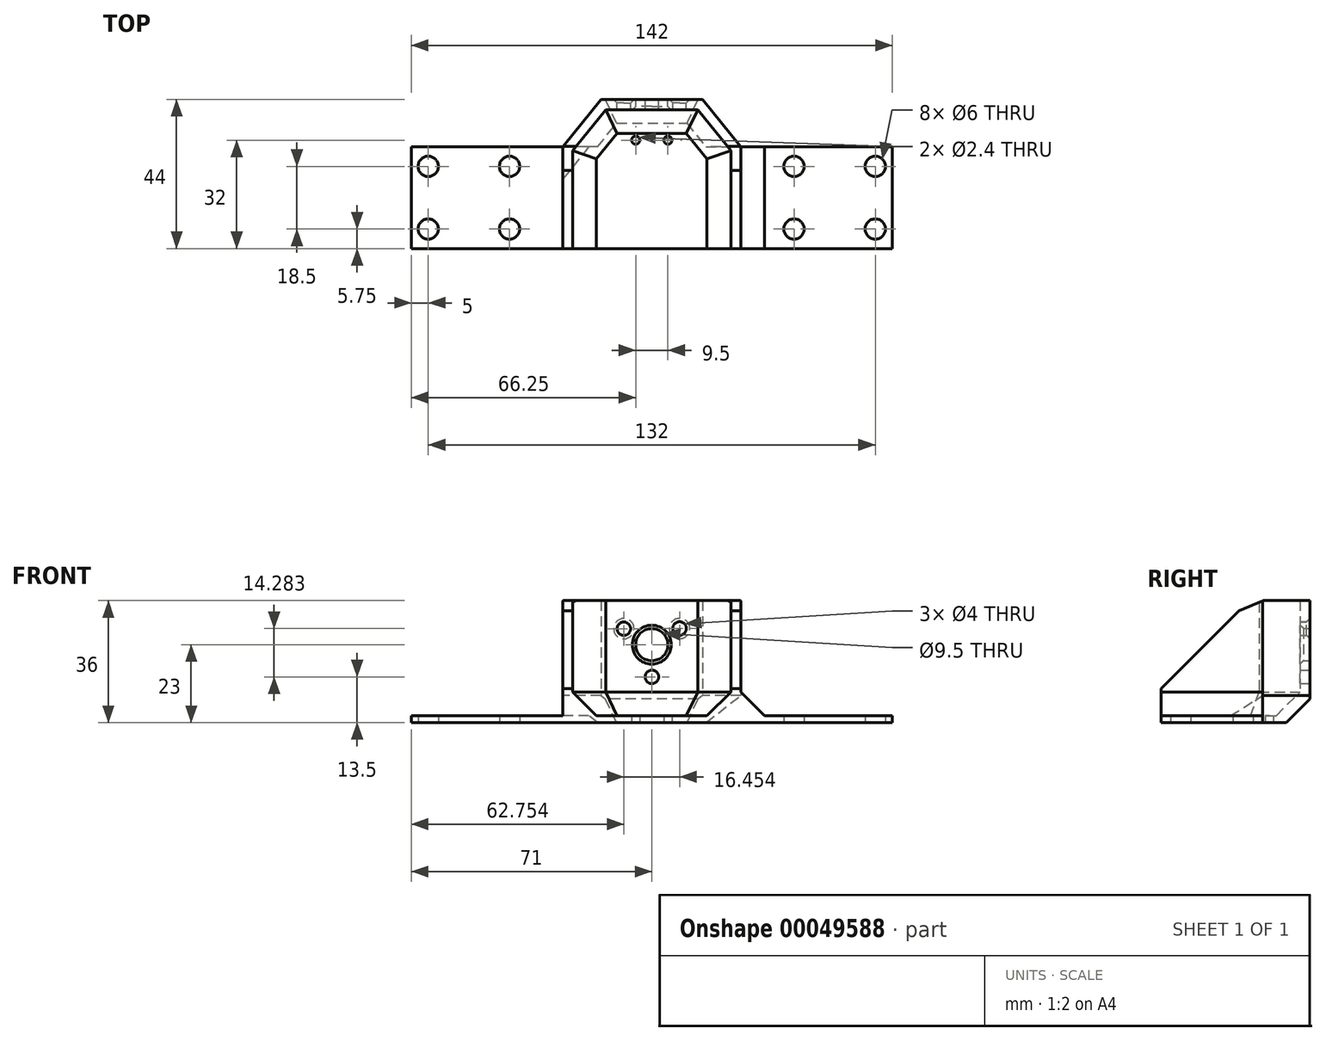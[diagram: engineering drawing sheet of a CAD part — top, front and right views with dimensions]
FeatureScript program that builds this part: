
annotation { "Feature Type Name" : "Feature", "Feature Type Description" : "" }
export const myFeature = defineFeature(function(context is Context, id is Id, definition is map)
    precondition{}
    {
        {
            var Q0;
            Q0=qCreatedBy(makeId("Top.planeOp"),FACE);
            var sketch = newSketch(context, id + "F0", { "sketchPlane" : qUnion([Q0])});
            skPoint(sketch, "E0.rect.middle", {"position": v(0, 0) * mm});
            skCircle(sketch, "E1", {"center": v(-42, 9.25) * mm, "radius": 3 * mm});
            skCircle(sketch, "E2", {"center": v(-66, 9.25) * mm, "radius": 3 * mm});
            skCircle(sketch, "E3", {"center": v(-66, -9.25) * mm, "radius": 3 * mm});
            skCircle(sketch, "E4", {"center": v(-42, -9.25) * mm, "radius": 3 * mm});
            skCircle(sketch, "E5", {"center": v(42, -9.25) * mm, "radius": 3 * mm});
            skCircle(sketch, "E6", {"center": v(66, -9.25) * mm, "radius": 3 * mm});
            skCircle(sketch, "E7", {"center": v(66, 9.25) * mm, "radius": 3 * mm});
            skCircle(sketch, "E8", {"center": v(42, 9.25) * mm, "radius": 3 * mm});
            skLineSegment(sketch, "E9.rect.bottom", {"start": v(71, -15) * mm, "end": v(-71, -15) * mm});
            skLineSegment(sketch, "E9.rect.top", {"start": v(71, 15) * mm, "end": v(26.31, 15) * mm});
            skLineSegment(sketch, "E9.rect.left", {"start": v(71, -15) * mm, "end": v(71, 15) * mm});
            skLineSegment(sketch, "E9.rect.right", {"start": v(-71, -15) * mm, "end": v(-71, 15) * mm});
            skLineSegment(sketch, "E10.rect.bottom", {"start": v(15, 29) * mm, "end": v(-15, 29) * mm});
            skPoint(sketch, "E10.rect.middle", {"position": v(0, 15) * mm});
            skPoint(sketch, "E10.rect.top.start.orphan", {"position": v(15, 1) * mm});
            skPoint(sketch, "E11.orphan", {"position": v(-15, 1) * mm});
            skLineSegment(sketch, "E12.trimOffspring", {"start": v(-26.31, 15) * mm, "end": v(-71, 15) * mm});
            skLineSegment(sketch, "E13", {"start": v(-15, 29) * mm, "end": v(-26.31, 15) * mm});
            skLineSegment(sketch, "E14", {"start": v(15, 29) * mm, "end": v(26.31, 15) * mm});
            skSolve(sketch);
        }
        {
            var Q0;
            Q0=makeQuery(id+"F0.imprint","IMPRINT",FACE,{"disambiguationData":[TD([[makeQuery(id+"F0.imprint","IMPRINT",EDGE,{"derivedFrom":sQuery(id+"F0.wireOp",EDGE,"E1")}),-1.0]])]});
            extrude(context, id + "F1", {"entities" : qUnion([Q0]), "depth" : 2 * mm});
        }
        {
            var Q0;
            Q0=makeQuery(id+"F1.opExtrude","CAP_FACE",FACE,{"disambiguationData":[OSD([sQuery(id+"F0.wireOp",EDGE,"E1"),sQuery(id+"F0.wireOp",EDGE,"E2"),sQuery(id+"F0.wireOp",EDGE,"E3"),sQuery(id+"F0.wireOp",EDGE,"E4"),sQuery(id+"F0.wireOp",EDGE,"E5"),sQuery(id+"F0.wireOp",EDGE,"E6"),sQuery(id+"F0.wireOp",EDGE,"E7"),sQuery(id+"F0.wireOp",EDGE,"E8"),sQuery(id+"F0.wireOp",EDGE,"E9.rect.bottom"),sQuery(id+"F0.wireOp",EDGE,"E9.rect.top"),sQuery(id+"F0.wireOp",EDGE,"E9.rect.left"),sQuery(id+"F0.wireOp",EDGE,"E9.rect.right"),sQuery(id+"F0.wireOp",EDGE,"E10.rect.bottom"),sQuery(id+"F0.wireOp",EDGE,"E12.trimOffspring"),sQuery(id+"F0.wireOp",EDGE,"E13"),sQuery(id+"F0.wireOp",EDGE,"E14")])],"isStart":false});
            var sketch = newSketch(context, id + "F2", { "sketchPlane" : qUnion([Q0])});
            skLineSegment(sketch, "E15", {"start": v(-26.31, 15) * mm, "end": v(-26.31, -15) * mm});
            skLineSegment(sketch, "E16", {"start": v(26.31, 15) * mm, "end": v(26.31, -15) * mm});
            skLineSegment(sketch, "E17.0", {"start": v(-23.31, 13.94) * mm, "end": v(-23.31, -15) * mm});
            skLineSegment(sketch, "E17.1", {"start": v(23.31, 13.94) * mm, "end": v(23.31, -15) * mm});
            skLineSegment(sketch, "E17.2", {"start": v(13.57, 26) * mm, "end": v(23.31, 13.94) * mm});
            skLineSegment(sketch, "E17.3", {"start": v(13.57, 26) * mm, "end": v(-13.57, 26) * mm});
            skLineSegment(sketch, "E17.4", {"start": v(-13.57, 26) * mm, "end": v(-23.31, 13.94) * mm});
            skSolve(sketch);
        }
        {
            var Q0;
            {var subQ2=sQuery(id+"F2.wireOp",EDGE,"E15");Q0=makeQuery(id+"F2.imprint","IMPRINT",FACE,{"disambiguationData":[TD([[makeQuery(id+"F2.imprint","IMPRINT",EDGE,{"derivedFrom":subQ2}),1.0]])]});}
            extrude(context, id + "F3", {"entities" : qUnion([Q0]), "operationType" : NewBodyOperationType.ADD, "depth" : 21 * mm});
        }
        {
            var Q0;
            {var subQ0=sQuery(id+"F0.wireOp",EDGE,"E10.rect.bottom");Q0=makeQuery(id+"F3.boolean.opBoolean","MERGE",FACE,{"derivedFrom":[makeQuery(id+"F1.opExtrude","SWEPT_FACE",FACE,{"disambiguationData":[OSD([subQ0])]}),makeQuery(id+"F3.opExtrude","SWEPT_FACE",FACE,{"disambiguationData":[OSD([subQ0])]})]});}
            var sketch = newSketch(context, id + "F4", { "sketchPlane" : qUnion([Q0])});
            skCircle(sketch, "E18", {"center": v(0, 23) * mm, "radius": 4.75 * mm});
            skLineSegment(sketch, "E19", {"start": v(0, 36) * mm, "end": v(-15, 36) * mm});
            skLineSegment(sketch, "E20", {"start": v(-15, 36) * mm, "end": v(-15, 23) * mm});
            skLineSegment(sketch, "E21", {"start": v(0, 36) * mm, "end": v(15, 36) * mm});
            skLineSegment(sketch, "E22", {"start": v(15, 36) * mm, "end": v(15, 23) * mm});
            skLineSegment(sketch, "E23", {"start": v(-15, 23) * mm, "end": v(-4.75, 23) * mm});
            skLineSegment(sketch, "E24.trimOffspring", {"start": v(4.75, 23) * mm, "end": v(15, 23) * mm});
            skCircle(sketch, "E25.cCircle", {"center": v(0, 23) * mm, "radius": 4.84 * mm, "construction": true});
            skPoint(sketch, "E25.0.midPoint", {"position": v(0, 18.16) * mm});
            skCircle(sketch, "E26", {"center": v(8.25, 27.72) * mm, "radius": 2 * mm});
            skCircle(sketch, "E27.1.0", {"center": v(-8.2, 27.78) * mm, "radius": 2 * mm});
            skCircle(sketch, "E27.2.0", {"center": v(-0.04, 13.5) * mm, "radius": 2 * mm});
            skPoint(sketch, "E25.0.start.orphan", {"position": v(8.38, 18.16) * mm});
            skPoint(sketch, "E25.1.start.orphan", {"position": v(-8.37, 18.16) * mm});
            skSolve(sketch);
        }
        {
            var Q0;
            Q0=makeQuery(id+"F4.imprint","IMPRINT",FACE,{"disambiguationData":[TD([[makeQuery(id+"F4.imprint","IMPRINT",EDGE,{"derivedFrom":sQuery(id+"F4.wireOp",EDGE,"E19")}),1.0]])]});
            extrude(context, id + "F5", {"entities" : qUnion([Q0]), "operationType" : NewBodyOperationType.ADD, "oppositeDirection" : true, "depth" : 3 * mm});
        }
        {
            var Q0;
            Q0=makeQuery(id+"F4.imprint","IMPRINT",FACE,{"disambiguationData":[TD([[makeQuery(id+"F4.imprint","IMPRINT",EDGE,{"derivedFrom":sQuery(id+"F4.wireOp",EDGE,"E27.1.0")}),1.0]])]});
            var Q1;
            {var subQ0=makeQuery(id+"F3.opExtrude","CAP_EDGE",EDGE,{"disambiguationData":[OSD([sQuery(id+"F0.wireOp",EDGE,"E10.rect.bottom")])],"isStart":false});var subQ1=sQuery(id+"F4.wireOp",EDGE,"E18");var subQ3=makeQuery(id+"F4.imprint","INTERSECT",VERTEX,{"derivedFrom":[subQ0,subQ1,sQuery(id+"F4.wireOp",EDGE,"E23")]});Q1=makeQuery(id+"F4.imprint","IMPRINT",FACE,{"disambiguationData":[TD([[makeQuery(id+"F4.imprint","IMPRINT",EDGE,{"disambiguationData":[TD([[subQ3,-1.0]])],"derivedFrom":subQ1}),1.0]])]});}
            var Q2;
            Q2=makeQuery(id+"F4.imprint","IMPRINT",FACE,{"disambiguationData":[TD([[makeQuery(id+"F4.imprint","IMPRINT",EDGE,{"derivedFrom":sQuery(id+"F4.wireOp",EDGE,"E27.2.0")}),1.0]])]});
            extrude(context, id + "F6", {"entities" : qUnion([Q0, Q1, Q2]), "operationType" : NewBodyOperationType.REMOVE, "endBound" : BoundingType.THROUGH_ALL, "oppositeDirection" : true, "depth" : 25 * mm});
        }
        {
            var Q0;
            Q0=makeQuery(id+"F3.opExtrude","CAP_EDGE",EDGE,{"disambiguationData":[OSD([sQuery(id+"F2.wireOp",EDGE,"E15")])],"isStart":true});
            var Q1;
            Q1=makeQuery(id+"F3.opExtrude","CAP_EDGE",EDGE,{"disambiguationData":[OSD([sQuery(id+"F2.wireOp",EDGE,"E17.1")])],"isStart":true});
            var Q2;
            Q2=makeQuery(id+"F3.opExtrude","CAP_EDGE",EDGE,{"disambiguationData":[OSD([sQuery(id+"F2.wireOp",EDGE,"E17.2")])],"isStart":true});
            var Q3;
            Q3=makeQuery(id+"F3.opExtrude","CAP_EDGE",EDGE,{"disambiguationData":[OSD([sQuery(id+"F2.wireOp",EDGE,"E17.4")])],"isStart":true});
            var Q4;
            Q4=makeQuery(id+"F3.opExtrude","CAP_EDGE",EDGE,{"disambiguationData":[OSD([sQuery(id+"F2.wireOp",EDGE,"E17.0")])],"isStart":true});
            var Q5;
            Q5=makeQuery(id+"F3.opExtrude","CAP_EDGE",EDGE,{"disambiguationData":[OSD([sQuery(id+"F2.wireOp",EDGE,"E16")])],"isStart":true});
            var Q6;
            Q6=makeQuery(id+"F3.opExtrude","CAP_EDGE",EDGE,{"disambiguationData":[OSD([sQuery(id+"F2.wireOp",EDGE,"E17.3")])],"isStart":true});
            var Q7;
            Q7=makeQuery(id+"F1.opExtrude","CAP_EDGE",EDGE,{"disambiguationData":[OSD([sQuery(id+"F0.wireOp",EDGE,"E10.rect.bottom")])],"isStart":true});
            chamfer(context, id + "F7", {"entities" : qUnion([Q0, Q1, Q2, Q3, Q4, Q5, Q6, Q7]), "width" : 7 * mm, "tangentPropagation" : true});
        }
        {
            var Q0;
            {var subQ0=sQuery(id+"F0.wireOp",EDGE,"E9.rect.bottom");var subQ1=sQuery(id+"F0.wireOp",EDGE,"E10.rect.bottom");var subQ2=sQuery(id+"F0.wireOp",EDGE,"E13");var subQ3=sQuery(id+"F2.wireOp",EDGE,"E15");var subQ4=sQuery(id+"F2.wireOp",EDGE,"E16");var subQ5=sQuery(id+"F2.wireOp",EDGE,"E17.0");var subQ6=sQuery(id+"F2.wireOp",EDGE,"E17.1");var subQ7=sQuery(id+"F2.wireOp",EDGE,"E17.3");var subQ8=sQuery(id+"F2.wireOp",EDGE,"E17.4");Q0=makeQuery(id+"F5.boolean.opBoolean","SPLIT",FACE,{"disambiguationData":[TD([makeQuery(id+"F1.opExtrude","SWEPT_FACE",FACE,{"disambiguationData":[OSD([subQ2])]})])],"derivedFrom":makeQuery(id+"F3.opExtrude","CAP_FACE",FACE,{"disambiguationData":[OSD([subQ0,subQ1,subQ2,sQuery(id+"F0.wireOp",EDGE,"E14"),subQ3,subQ4,subQ5,subQ6,sQuery(id+"F2.wireOp",EDGE,"E17.2"),subQ7,subQ8])],"isStart":false})});}
            var Q1;
            {var subQ0=sQuery(id+"F0.wireOp",EDGE,"E9.rect.bottom");var subQ1=sQuery(id+"F0.wireOp",EDGE,"E10.rect.bottom");var subQ2=sQuery(id+"F0.wireOp",EDGE,"E14");var subQ3=sQuery(id+"F2.wireOp",EDGE,"E15");var subQ4=sQuery(id+"F2.wireOp",EDGE,"E16");var subQ5=sQuery(id+"F2.wireOp",EDGE,"E17.0");var subQ6=sQuery(id+"F2.wireOp",EDGE,"E17.1");var subQ7=sQuery(id+"F2.wireOp",EDGE,"E17.2");var subQ8=sQuery(id+"F2.wireOp",EDGE,"E17.3");Q1=makeQuery(id+"F5.boolean.opBoolean","SPLIT",FACE,{"disambiguationData":[TD([makeQuery(id+"F1.opExtrude","SWEPT_FACE",FACE,{"disambiguationData":[OSD([subQ2])]})])],"derivedFrom":makeQuery(id+"F3.opExtrude","CAP_FACE",FACE,{"disambiguationData":[OSD([subQ0,subQ1,sQuery(id+"F0.wireOp",EDGE,"E13"),subQ2,subQ3,subQ4,subQ5,subQ6,subQ7,subQ8,sQuery(id+"F2.wireOp",EDGE,"E17.4")])],"isStart":false})});}
            extrude(context, id + "F8", {"entities" : qUnion([Q0, Q1]), "operationType" : NewBodyOperationType.ADD, "depth" : 13 * mm});
        }
        {
            var Q0;
            {var subQ0=sQuery(id+"F0.wireOp",EDGE,"E9.rect.bottom");var subQ1=makeQuery(id+"F1.opExtrude","CAP_EDGE",EDGE,{"disambiguationData":[OSD([subQ0])],"isStart":false});Q0=makeQuery(id+"F8.opExtrude","CAP_EDGE",EDGE,{"disambiguationData":[OSD([subQ0]),TDD([makeQuery(id+"F3.opExtrude","CAP_EDGE",EDGE,{"disambiguationData":[OSD([subQ0]),TDD([makeQuery(id+"F2.imprint","IMPRINT",EDGE,{"disambiguationData":[TD([[makeQuery(id+"F2.imprint","INTERSECT",VERTEX,{"derivedFrom":[subQ1,sQuery(id+"F2.wireOp",EDGE,"E15")]}),1.0]])],"derivedFrom":subQ1})])],"isStart":false})])],"isStart":false});}
            var Q1;
            {var subQ0=sQuery(id+"F0.wireOp",EDGE,"E9.rect.bottom");var subQ1=makeQuery(id+"F1.opExtrude","CAP_EDGE",EDGE,{"disambiguationData":[OSD([subQ0])],"isStart":false});Q1=makeQuery(id+"F8.opExtrude","CAP_EDGE",EDGE,{"disambiguationData":[OSD([subQ0]),TDD([makeQuery(id+"F3.opExtrude","CAP_EDGE",EDGE,{"disambiguationData":[OSD([subQ0]),TDD([makeQuery(id+"F2.imprint","IMPRINT",EDGE,{"disambiguationData":[TD([[makeQuery(id+"F2.imprint","INTERSECT",VERTEX,{"derivedFrom":[subQ1,sQuery(id+"F2.wireOp",EDGE,"E16")]}),-1.0]])],"derivedFrom":subQ1})])],"isStart":false})])],"isStart":false});}
            chamfer(context, id + "F9", {"entities" : qUnion([Q0, Q1]), "width" : 26 * mm, "tangentPropagation" : true});
        }
        {
            var Q0;
            {var subQ0=sQuery(id+"F0.wireOp",EDGE,"E9.rect.bottom");var subQ1=makeQuery(id+"F1.opExtrude","CAP_EDGE",EDGE,{"disambiguationData":[OSD([subQ0])],"isStart":false});var subQ2=sQuery(id+"F2.wireOp",EDGE,"E17.0");var subQ3=sQuery(id+"F2.wireOp",EDGE,"E15");var subQ4=makeQuery(id+"F2.imprint","IMPRINT",EDGE,{"disambiguationData":[TD([[makeQuery(id+"F2.imprint","INTERSECT",VERTEX,{"derivedFrom":[subQ1,subQ3]}),1.0]])],"derivedFrom":subQ1});var subQ5=sQuery(id+"F4.wireOp",EDGE,"E19");var subQ6=sQuery(id+"F4.wireOp",EDGE,"E21");var subQ7=sQuery(id+"F0.wireOp",EDGE,"E10.rect.bottom");var subQ8=sQuery(id+"F0.wireOp",EDGE,"E13");var subQ9=sQuery(id+"F0.wireOp",EDGE,"E14");var subQ10=sQuery(id+"F2.wireOp",EDGE,"E16");var subQ11=sQuery(id+"F2.wireOp",EDGE,"E17.1");var subQ12=sQuery(id+"F2.wireOp",EDGE,"E17.2");var subQ13=sQuery(id+"F2.wireOp",EDGE,"E17.3");var subQ14=sQuery(id+"F2.wireOp",EDGE,"E17.4");var subQ15=makeQuery(id+"F3.opExtrude","CAP_FACE",FACE,{"disambiguationData":[OSD([subQ0,subQ7,subQ8,subQ9,subQ3,subQ10,subQ2,subQ11,subQ12,subQ13,subQ14])],"isStart":false});Q0=makeQuery(id+"F9.opChamfer","BLEND_EDGE",EDGE,{"blendedFrom":[makeQuery(id+"F8.opExtrude","CAP_EDGE",EDGE,{"disambiguationData":[OSD([subQ0]),TDD([makeQuery(id+"F3.opExtrude","CAP_EDGE",EDGE,{"disambiguationData":[OSD([subQ0]),TDD([subQ4])],"isStart":false})])],"isStart":false}),makeQuery(id+"F8.boolean.opBoolean","MERGE",FACE,{"derivedFrom":[makeQuery(id+"F5.opExtrude","SWEPT_FACE",FACE,{"disambiguationData":[OSD([subQ5,subQ6])]}),makeQuery(id+"F8.opExtrude","CAP_FACE",FACE,{"disambiguationData":[OSD([subQ0,subQ7,subQ8,subQ9,subQ3,subQ10,subQ2,subQ11,subQ12,subQ13,subQ14]),TDD([makeQuery(id+"F5.boolean.opBoolean","SPLIT",FACE,{"disambiguationData":[TD([makeQuery(id+"F1.opExtrude","SWEPT_FACE",FACE,{"disambiguationData":[OSD([subQ8])]})])],"derivedFrom":subQ15})])],"isStart":false}),makeQuery(id+"F8.opExtrude","CAP_FACE",FACE,{"disambiguationData":[OSD([subQ0,subQ7,subQ8,subQ9,subQ3,subQ10,subQ2,subQ11,subQ12,subQ13,subQ14]),TDD([makeQuery(id+"F5.boolean.opBoolean","SPLIT",FACE,{"disambiguationData":[TD([makeQuery(id+"F1.opExtrude","SWEPT_FACE",FACE,{"disambiguationData":[OSD([subQ9])]})])],"derivedFrom":subQ15})])],"isStart":false})]})],"blendedInto":[makeQuery(id+"F8.boolean.opBoolean","MERGE",FACE,{"derivedFrom":[makeQuery(id+"F5.opExtrude","SWEPT_FACE",FACE,{"disambiguationData":[OSD([subQ5,subQ6])]}),makeQuery(id+"F8.opExtrude","CAP_FACE",FACE,{"disambiguationData":[OSD([subQ0,subQ7,subQ8,subQ9,subQ3,subQ10,subQ2,subQ11,subQ12,subQ13,subQ14]),TDD([makeQuery(id+"F5.boolean.opBoolean","SPLIT",FACE,{"disambiguationData":[TD([makeQuery(id+"F1.opExtrude","SWEPT_FACE",FACE,{"disambiguationData":[OSD([subQ8])]})])],"derivedFrom":subQ15})])],"isStart":false}),makeQuery(id+"F8.opExtrude","CAP_FACE",FACE,{"disambiguationData":[OSD([subQ0,subQ7,subQ8,subQ9,subQ3,subQ10,subQ2,subQ11,subQ12,subQ13,subQ14]),TDD([makeQuery(id+"F5.boolean.opBoolean","SPLIT",FACE,{"disambiguationData":[TD([makeQuery(id+"F1.opExtrude","SWEPT_FACE",FACE,{"disambiguationData":[OSD([subQ9])]})])],"derivedFrom":subQ15})])],"isStart":false})]})]});}
            var Q1;
            {var subQ0=sQuery(id+"F0.wireOp",EDGE,"E9.rect.bottom");var subQ1=makeQuery(id+"F1.opExtrude","CAP_EDGE",EDGE,{"disambiguationData":[OSD([subQ0])],"isStart":false});var subQ2=sQuery(id+"F2.wireOp",EDGE,"E17.1");var subQ3=sQuery(id+"F2.wireOp",EDGE,"E16");var subQ4=makeQuery(id+"F2.imprint","IMPRINT",EDGE,{"disambiguationData":[TD([[makeQuery(id+"F2.imprint","INTERSECT",VERTEX,{"derivedFrom":[subQ1,subQ3]}),-1.0]])],"derivedFrom":subQ1});var subQ5=sQuery(id+"F4.wireOp",EDGE,"E19");var subQ6=sQuery(id+"F4.wireOp",EDGE,"E21");var subQ7=sQuery(id+"F0.wireOp",EDGE,"E10.rect.bottom");var subQ8=sQuery(id+"F0.wireOp",EDGE,"E13");var subQ9=sQuery(id+"F0.wireOp",EDGE,"E14");var subQ10=sQuery(id+"F2.wireOp",EDGE,"E15");var subQ11=sQuery(id+"F2.wireOp",EDGE,"E17.0");var subQ12=sQuery(id+"F2.wireOp",EDGE,"E17.2");var subQ13=sQuery(id+"F2.wireOp",EDGE,"E17.3");var subQ14=sQuery(id+"F2.wireOp",EDGE,"E17.4");var subQ15=makeQuery(id+"F3.opExtrude","CAP_FACE",FACE,{"disambiguationData":[OSD([subQ0,subQ7,subQ8,subQ9,subQ10,subQ3,subQ11,subQ2,subQ12,subQ13,subQ14])],"isStart":false});Q1=makeQuery(id+"F9.opChamfer","BLEND_EDGE",EDGE,{"blendedFrom":[makeQuery(id+"F8.opExtrude","CAP_EDGE",EDGE,{"disambiguationData":[OSD([subQ0]),TDD([makeQuery(id+"F3.opExtrude","CAP_EDGE",EDGE,{"disambiguationData":[OSD([subQ0]),TDD([subQ4])],"isStart":false})])],"isStart":false}),makeQuery(id+"F8.boolean.opBoolean","MERGE",FACE,{"derivedFrom":[makeQuery(id+"F5.opExtrude","SWEPT_FACE",FACE,{"disambiguationData":[OSD([subQ5,subQ6])]}),makeQuery(id+"F8.opExtrude","CAP_FACE",FACE,{"disambiguationData":[OSD([subQ0,subQ7,subQ8,subQ9,subQ10,subQ3,subQ11,subQ2,subQ12,subQ13,subQ14]),TDD([makeQuery(id+"F5.boolean.opBoolean","SPLIT",FACE,{"disambiguationData":[TD([makeQuery(id+"F1.opExtrude","SWEPT_FACE",FACE,{"disambiguationData":[OSD([subQ8])]})])],"derivedFrom":subQ15})])],"isStart":false}),makeQuery(id+"F8.opExtrude","CAP_FACE",FACE,{"disambiguationData":[OSD([subQ0,subQ7,subQ8,subQ9,subQ10,subQ3,subQ11,subQ2,subQ12,subQ13,subQ14]),TDD([makeQuery(id+"F5.boolean.opBoolean","SPLIT",FACE,{"disambiguationData":[TD([makeQuery(id+"F1.opExtrude","SWEPT_FACE",FACE,{"disambiguationData":[OSD([subQ9])]})])],"derivedFrom":subQ15})])],"isStart":false})]})],"blendedInto":[makeQuery(id+"F8.boolean.opBoolean","MERGE",FACE,{"derivedFrom":[makeQuery(id+"F5.opExtrude","SWEPT_FACE",FACE,{"disambiguationData":[OSD([subQ5,subQ6])]}),makeQuery(id+"F8.opExtrude","CAP_FACE",FACE,{"disambiguationData":[OSD([subQ0,subQ7,subQ8,subQ9,subQ10,subQ3,subQ11,subQ2,subQ12,subQ13,subQ14]),TDD([makeQuery(id+"F5.boolean.opBoolean","SPLIT",FACE,{"disambiguationData":[TD([makeQuery(id+"F1.opExtrude","SWEPT_FACE",FACE,{"disambiguationData":[OSD([subQ8])]})])],"derivedFrom":subQ15})])],"isStart":false}),makeQuery(id+"F8.opExtrude","CAP_FACE",FACE,{"disambiguationData":[OSD([subQ0,subQ7,subQ8,subQ9,subQ10,subQ3,subQ11,subQ2,subQ12,subQ13,subQ14]),TDD([makeQuery(id+"F5.boolean.opBoolean","SPLIT",FACE,{"disambiguationData":[TD([makeQuery(id+"F1.opExtrude","SWEPT_FACE",FACE,{"disambiguationData":[OSD([subQ9])]})])],"derivedFrom":subQ15})])],"isStart":false})]})]});}
            chamfer(context, id + "F10", {"entities" : qUnion([Q0, Q1]), "width" : 10 * mm, "tangentPropagation" : true});
        }
        {
            var Q0;
            Q0=makeQuery(id+"F1.opExtrude","CAP_EDGE",EDGE,{"disambiguationData":[OSD([sQuery(id+"F0.wireOp",EDGE,"E14")])],"isStart":true});
            var Q1;
            Q1=makeQuery(id+"F1.opExtrude","CAP_EDGE",EDGE,{"disambiguationData":[OSD([sQuery(id+"F0.wireOp",EDGE,"E13")])],"isStart":true});
            chamfer(context, id + "F11", {"entities" : qUnion([Q0, Q1]), "width" : 8 * mm, "tangentPropagation" : true});
        }
        {
            var Q0;
            Q0=makeQuery(id+"F6.boolean.opBoolean","COPY",EDGE,{"derivedFrom":makeQuery(id+"F6.opExtrude","CAP_EDGE",EDGE,{"disambiguationData":[OSD([sQuery(id+"F4.wireOp",EDGE,"E27.2.0")])],"isStart":true})});
            var Q1;
            Q1=makeQuery(id+"F6.boolean.opBoolean","COPY",EDGE,{"derivedFrom":makeQuery(id+"F6.opExtrude","CAP_EDGE",EDGE,{"disambiguationData":[OSD([sQuery(id+"F4.wireOp",EDGE,"E27.1.0")])],"isStart":true})});
            var Q2;
            Q2=makeQuery(id+"F5.opExtrude","CAP_EDGE",EDGE,{"disambiguationData":[OSD([sQuery(id+"F4.wireOp",EDGE,"E26")])],"isStart":true});
            var Q3;
            Q3=makeQuery(id+"F5.opExtrude","CAP_EDGE",EDGE,{"disambiguationData":[OSD([sQuery(id+"F4.wireOp",EDGE,"E27.1.0")])],"isStart":true});
            chamfer(context, id + "F12", {"entities" : qUnion([Q0, Q1, Q2, Q3]), "width" : 1 * mm, "tangentPropagation" : true});
        }
        {
            var Q0;
            {var subQ0=sQuery(id+"F4.wireOp",EDGE,"E18");Q0=makeQuery(id+"F6.boolean.opBoolean","INTERSECT",EDGE,{"derivedFrom":[makeQuery(id+"F5.boolean.opBoolean","MERGE",FACE,{"derivedFrom":[makeQuery(id+"F3.opExtrude","SWEPT_FACE",FACE,{"disambiguationData":[OSD([sQuery(id+"F2.wireOp",EDGE,"E17.3")])]}),makeQuery(id+"F5.opExtrude","CAP_FACE",FACE,{"disambiguationData":[OSD([subQ0,sQuery(id+"F4.wireOp",EDGE,"E19"),sQuery(id+"F4.wireOp",EDGE,"E20"),sQuery(id+"F4.wireOp",EDGE,"E21"),sQuery(id+"F4.wireOp",EDGE,"E22"),sQuery(id+"F4.wireOp",EDGE,"E23"),sQuery(id+"F4.wireOp",EDGE,"E24.trimOffspring"),sQuery(id+"F4.wireOp",EDGE,"E26"),sQuery(id+"F4.wireOp",EDGE,"E27.1.0")])],"isStart":false})]}),makeQuery(id+"F6.opExtrude","SWEPT_FACE",FACE,{"disambiguationData":[OSD([subQ0])]})]});}
            var Q1;
            {var subQ0=sQuery(id+"F4.wireOp",EDGE,"E18");Q1=makeQuery(id+"F6.boolean.opBoolean","MERGE",EDGE,{"derivedFrom":[makeQuery(id+"F5.opExtrude","CAP_EDGE",EDGE,{"disambiguationData":[OSD([subQ0])],"isStart":true}),makeQuery(id+"F6.opExtrude","CAP_EDGE",EDGE,{"disambiguationData":[OSD([subQ0])],"isStart":true})]});}
            chamfer(context, id + "F13", {"entities" : qUnion([Q0, Q1]), "width" : 1 * mm, "tangentPropagation" : true});
        }
        {
            var Q0;
            Q0=makeQuery(id+"F1.opExtrude","CAP_FACE",FACE,{"disambiguationData":[OSD([sQuery(id+"F0.wireOp",EDGE,"E1"),sQuery(id+"F0.wireOp",EDGE,"E2"),sQuery(id+"F0.wireOp",EDGE,"E3"),sQuery(id+"F0.wireOp",EDGE,"E4"),sQuery(id+"F0.wireOp",EDGE,"E5"),sQuery(id+"F0.wireOp",EDGE,"E6"),sQuery(id+"F0.wireOp",EDGE,"E7"),sQuery(id+"F0.wireOp",EDGE,"E8"),sQuery(id+"F0.wireOp",EDGE,"E9.rect.bottom"),sQuery(id+"F0.wireOp",EDGE,"E9.rect.top"),sQuery(id+"F0.wireOp",EDGE,"E9.rect.left"),sQuery(id+"F0.wireOp",EDGE,"E9.rect.right"),sQuery(id+"F0.wireOp",EDGE,"E10.rect.bottom"),sQuery(id+"F0.wireOp",EDGE,"E12.trimOffspring"),sQuery(id+"F0.wireOp",EDGE,"E13"),sQuery(id+"F0.wireOp",EDGE,"E14")])],"isStart":true});
            var sketch = newSketch(context, id + "F14", { "sketchPlane" : qUnion([Q0])});
            skLineSegment(sketch, "E28", {"start": v(0, -22) * mm, "end": v(0, -17) * mm});
            skLineSegment(sketch, "E29", {"start": v(0, -17) * mm, "end": v(4.75, -17) * mm});
            skLineSegment(sketch, "E30", {"start": v(0, -17) * mm, "end": v(-4.75, -17) * mm});
            skCircle(sketch, "E31", {"center": v(-4.75, -17) * mm, "radius": 1.2 * mm});
            skCircle(sketch, "E32", {"center": v(4.75, -17) * mm, "radius": 1.2 * mm});
            skSolve(sketch);
        }
        {
            var Q0;
            Q0=makeQuery(id+"F14.imprint","IMPRINT",FACE,{"disambiguationData":[TD([[makeQuery(id+"F14.imprint","IMPRINT",EDGE,{"derivedFrom":sQuery(id+"F14.wireOp",EDGE,"E31")}),1.0]])]});
            var Q1;
            Q1=makeQuery(id+"F14.imprint","IMPRINT",FACE,{"disambiguationData":[TD([[makeQuery(id+"F14.imprint","IMPRINT",EDGE,{"derivedFrom":sQuery(id+"F14.wireOp",EDGE,"E32")}),1.0]])]});
            var Q2;
            {var subQ0=sQuery(id+"F0.wireOp",EDGE,"E9.rect.bottom");var subQ3=sQuery(id+"F2.wireOp",EDGE,"E17.0");Q2=makeQuery(id+"F3.boolean.opBoolean","SPLIT",FACE,{"disambiguationData":[TD([makeQuery(id+"F3.opExtrude","SWEPT_FACE",FACE,{"disambiguationData":[OSD([subQ3])]})])],"derivedFrom":makeQuery(id+"F1.opExtrude","CAP_FACE",FACE,{"disambiguationData":[OSD([sQuery(id+"F0.wireOp",EDGE,"E1"),sQuery(id+"F0.wireOp",EDGE,"E2"),sQuery(id+"F0.wireOp",EDGE,"E3"),sQuery(id+"F0.wireOp",EDGE,"E4"),sQuery(id+"F0.wireOp",EDGE,"E5"),sQuery(id+"F0.wireOp",EDGE,"E6"),sQuery(id+"F0.wireOp",EDGE,"E7"),sQuery(id+"F0.wireOp",EDGE,"E8"),subQ0,sQuery(id+"F0.wireOp",EDGE,"E9.rect.top"),sQuery(id+"F0.wireOp",EDGE,"E9.rect.left"),sQuery(id+"F0.wireOp",EDGE,"E9.rect.right"),sQuery(id+"F0.wireOp",EDGE,"E10.rect.bottom"),sQuery(id+"F0.wireOp",EDGE,"E12.trimOffspring"),sQuery(id+"F0.wireOp",EDGE,"E13"),sQuery(id+"F0.wireOp",EDGE,"E14")])],"isStart":false})});}
            extrude(context, id + "F15", {"entities" : qUnion([Q0, Q1]), "operationType" : NewBodyOperationType.REMOVE, "endBound" : BoundingType.UP_TO_SURFACE, "oppositeDirection" : true, "endBoundEntityFace" : qUnion([Q2]), "depth" : 2 * mm});
        }
    });
